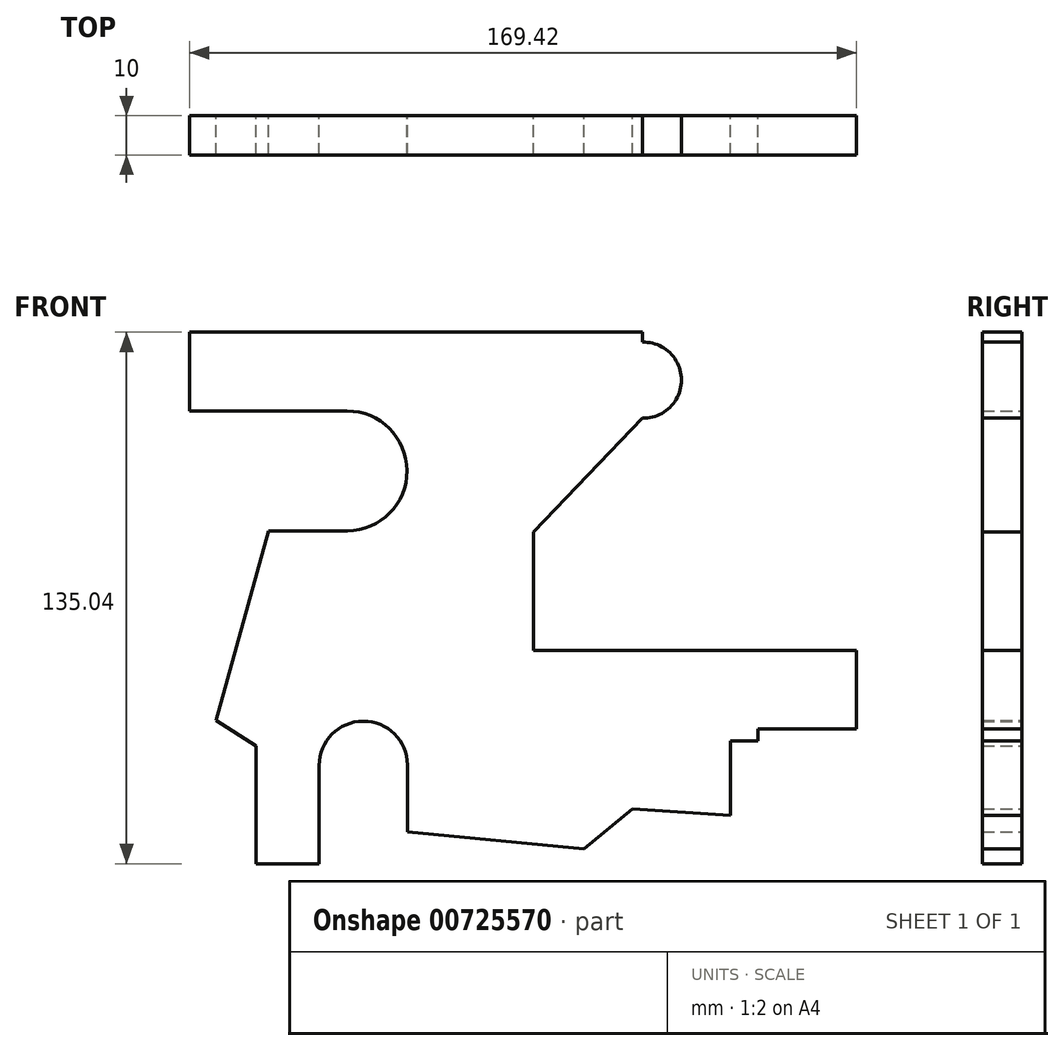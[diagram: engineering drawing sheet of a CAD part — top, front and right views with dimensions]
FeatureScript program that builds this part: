
annotation { "Feature Type Name" : "Feature", "Feature Type Description" : "" }
export const myFeature = defineFeature(function(context is Context, id is Id, definition is map)
    precondition{}
    {
        {
            var Q0;
            Q0=qCreatedBy(makeId("Front.planeOp"),FACE);
            var sketch = newSketch(context, id + "F0", { "sketchPlane" : qUnion([Q0])});
            skLineSegment(sketch, "E0", {"start": v(-73.42, 50.43) * mm, "end": v(41.58, 50.43) * mm});
            skLineSegment(sketch, "E1", {"start": v(41.58, 50.43) * mm, "end": v(41.58, 50.43) * mm});
            skLineSegment(sketch, "E2", {"start": v(41.58, 28.6) * mm, "end": v(14, -0.37) * mm});
            skLineSegment(sketch, "E3", {"start": v(14, -0.37) * mm, "end": v(14, -30.37) * mm});
            skLineSegment(sketch, "E4", {"start": v(14, -30.37) * mm, "end": v(96, -30.37) * mm});
            skLineSegment(sketch, "E5", {"start": v(96, -30.37) * mm, "end": v(96, -50.37) * mm});
            skLineSegment(sketch, "E6", {"start": v(96, -50.37) * mm, "end": v(71, -50.37) * mm});
            skLineSegment(sketch, "E7", {"start": v(71, -50.37) * mm, "end": v(71, -53.37) * mm});
            skLineSegment(sketch, "E8", {"start": v(71, -53.37) * mm, "end": v(64, -53.37) * mm});
            skLineSegment(sketch, "E9", {"start": v(64, -53.37) * mm, "end": v(64, -72.37) * mm});
            skLineSegment(sketch, "E10", {"start": v(64, -72.37) * mm, "end": v(39.05, -70.68) * mm});
            skLineSegment(sketch, "E11", {"start": v(39.05, -70.68) * mm, "end": v(26.72, -80.88) * mm});
            skLineSegment(sketch, "E12", {"start": v(26.72, -80.88) * mm, "end": v(-18.07, -76.53) * mm});
            skLineSegment(sketch, "E13", {"start": v(-40.52, -84.61) * mm, "end": v(-56.52, -84.61) * mm});
            skLineSegment(sketch, "E14", {"start": v(-56.52, -84.61) * mm, "end": v(-56.52, -54.61) * mm});
            skLineSegment(sketch, "E15", {"start": v(-56.52, -54.61) * mm, "end": v(-66.66, -48.2) * mm});
            skLineSegment(sketch, "E16", {"start": v(-66.66, -48.2) * mm, "end": v(-53.36, 0) * mm});
            skLineSegment(sketch, "E17", {"start": v(-73.42, 50.43) * mm, "end": v(-73.42, 30.43) * mm});
            skLineSegment(sketch, "E18", {"start": v(-73.42, 30.43) * mm, "end": v(-33.42, 30.43) * mm});
            skPoint(sketch, "E19.1.internal.orphan", {"position": v(-18.07, -66.44) * mm});
            skLineSegment(sketch, "E20", {"start": v(-18.07, -76.53) * mm, "end": v(-18.07, -59.53) * mm});
            skLineSegment(sketch, "E21", {"start": v(-40.52, -84.61) * mm, "end": v(-40.52, -59.61) * mm});
            skArc(sketch, "E22", {"start": v(-18.07, -59.53) * mm, "mid": v(-29.34, -48.39) * mm, "end": v(-40.52, -59.61) * mm});
            skLineSegment(sketch, "E23", {"start": v(-53.36, 0) * mm, "end": v(-33.36, 0) * mm});
            skArc(sketch, "E24", {"start": v(-33.36, 0) * mm, "mid": v(-18.2, 15.24) * mm, "end": v(-33.42, 30.43) * mm});
            skLineSegment(sketch, "E25", {"start": v(59.5, 45.98) * mm, "end": v(59.02, 45.98) * mm});
            skPoint(sketch, "E26.1.internal.orphan", {"position": v(52.69, 50.43) * mm});
            skLineSegment(sketch, "E27", {"start": v(41.58, 50.43) * mm, "end": v(41.58, 47.93) * mm});
            skArc(sketch, "E28", {"start": v(41.58, 28.6) * mm, "mid": v(51.53, 38.26) * mm, "end": v(41.58, 47.93) * mm});
            skSolve(sketch);
        }
        {
            var Q0;
            Q0=makeQuery(id+"F0.imprint","IMPRINT",FACE,{"disambiguationData":[TD([[makeQuery(id+"F0.imprint","IMPRINT",EDGE,{"derivedFrom":sQuery(id+"F0.wireOp",EDGE,"E0")}),-1.0]])]});
            extrude(context, id + "F1", {"entities" : qUnion([Q0]), "depth" : 10 * mm, "offsetDistance" : 25 * mm});
        }
    });
